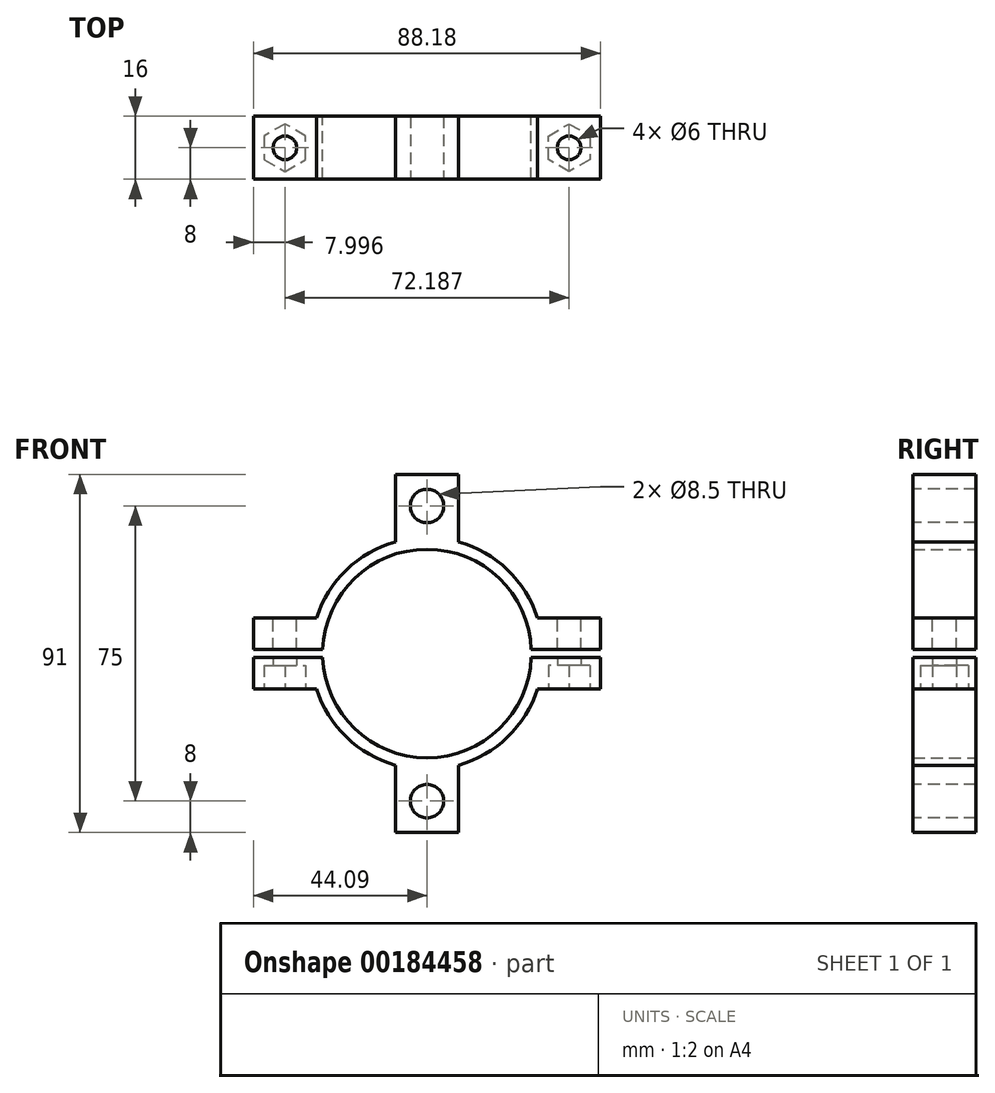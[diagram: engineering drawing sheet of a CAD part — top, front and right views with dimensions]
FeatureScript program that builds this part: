
annotation { "Feature Type Name" : "Feature", "Feature Type Description" : "" }
export const myFeature = defineFeature(function(context is Context, id is Id, definition is map)
    precondition{}
    {
        {
            var Q0;
            Q0=qCreatedBy(makeId("Front.planeOp"),FACE);
            var sketch = newSketch(context, id + "F0", { "sketchPlane" : qUnion([Q0])});
            skCircle(sketch, "E0", {"center": v(0, 0) * mm, "radius": 26.5 * mm, "construction": true});
            skLineSegment(sketch, "E1", {"start": v(-8, -45.5) * mm, "end": v(-8, -28.4) * mm});
            skArc(sketch, "E2", {"start": v(0, -26.5) * mm, "mid": v(-18.38, -19.09) * mm, "end": v(-26.48, -1) * mm});
            skLineSegment(sketch, "E3", {"start": v(-26.48, -1) * mm, "end": v(-44.1, -1) * mm});
            skLineSegment(sketch, "E4", {"start": v(-44.1, -1) * mm, "end": v(-44.1, -9) * mm});
            skLineSegment(sketch, "E5", {"start": v(-44.1, -9) * mm, "end": v(-28.1, -9) * mm});
            skArc(sketch, "E6", {"start": v(-28.1, -9) * mm, "mid": v(-20.49, -21.23) * mm, "end": v(-8, -28.4) * mm});
            skLineSegment(sketch, "E7", {"start": v(0, 0) * mm, "end": v(0, -39.44) * mm, "construction": true});
            skLineSegment(sketch, "E8", {"start": v(0, -45.5) * mm, "end": v(0, -26.5) * mm});
            skLineSegment(sketch, "E9", {"start": v(-8, -45.5) * mm, "end": v(0, -45.5) * mm});
            skSolve(sketch);
        }
        {
            var Q0;
            Q0=makeQuery(id+"F0.imprint","IMPRINT",FACE,{"disambiguationData":[TD([[makeQuery(id+"F0.imprint","IMPRINT",EDGE,{"derivedFrom":sQuery(id+"F0.wireOp",EDGE,"E1")}),-1.0]])]});
            extrude(context, id + "F1", {"entities" : qUnion([Q0]), "depth" : 16 * mm});
        }
        {
            var Q0;
            Q0=makeQuery(id+"F1.opExtrude","SWEPT_FACE",FACE,{"disambiguationData":[OSD([sQuery(id+"F0.wireOp",EDGE,"E5")])]});
            var sketch = newSketch(context, id + "F2", { "sketchPlane" : qUnion([Q0])});
            skLineSegment(sketch, "E10", {"start": v(-28.1, 8) * mm, "end": v(-44.1, 8) * mm, "construction": true});
            skLineSegment(sketch, "E11", {"start": v(-36.1, 16) * mm, "end": v(-36.1, 0) * mm, "construction": true});
            skCircle(sketch, "E12.cCircle", {"center": v(-36.1, 8) * mm, "radius": 5.25 * mm, "construction": true});
            skLineSegment(sketch, "E12.0", {"start": v(-36.1, 14.06) * mm, "end": v(-30.84, 11.03) * mm});
            skLineSegment(sketch, "E12.1", {"start": v(-30.84, 11.03) * mm, "end": v(-30.84, 4.97) * mm});
            skLineSegment(sketch, "E12.2", {"start": v(-30.84, 4.97) * mm, "end": v(-36.1, 1.94) * mm});
            skLineSegment(sketch, "E12.3", {"start": v(-36.1, 1.94) * mm, "end": v(-41.34, 4.97) * mm});
            skLineSegment(sketch, "E12.4", {"start": v(-41.34, 4.97) * mm, "end": v(-41.34, 11.03) * mm});
            skLineSegment(sketch, "E12.5", {"start": v(-41.34, 11.03) * mm, "end": v(-36.1, 14.06) * mm});
            skPoint(sketch, "E12.0.midPoint", {"position": v(-33.47, 12.55) * mm});
            skSolve(sketch);
        }
        {
            var Q0;
            Q0 = qSketchRegion(id + "F2", true);
            extrude(context, id + "F3", {"entities" : qUnion([Q0]), "operationType" : NewBodyOperationType.REMOVE, "oppositeDirection" : true, "depth" : 6 * mm});
        }
        {
            var Q0;
            Q0=makeQuery(id+"F3.boolean.opBoolean","COPY",FACE,{"derivedFrom":makeQuery(id+"F3.opExtrude","CAP_FACE",FACE,{"disambiguationData":[OSD([sQuery(id+"F2.wireOp",EDGE,"E12.0"),sQuery(id+"F2.wireOp",EDGE,"E12.1"),sQuery(id+"F2.wireOp",EDGE,"E12.2"),sQuery(id+"F2.wireOp",EDGE,"E12.3"),sQuery(id+"F2.wireOp",EDGE,"E12.4"),sQuery(id+"F2.wireOp",EDGE,"E12.5")])],"isStart":false})});
            var sketch = newSketch(context, id + "F4", { "sketchPlane" : qUnion([Q0])});
            skLineSegment(sketch, "E13", {"start": v(-30.84, 8) * mm, "end": v(-41.34, 8) * mm, "construction": true});
            skLineSegment(sketch, "E14", {"start": v(-36.1, 14.06) * mm, "end": v(-36.1, 1.94) * mm, "construction": true});
            skPoint(sketch, "E15", {"position": v(-36.1, 8) * mm});
            skSolve(sketch);
        }
        {
            var Q0;
            Q0=sQuery(id+"F4.wireOp",VERTEX,"E15");
            var Q1;
            Q1=makeQuery(id+"F1.opExtrude","SWEPT_BODY",BODY,{"disambiguationData":[OSD([sQuery(id+"F0.wireOp",EDGE,"LuoD2EtT-gfBr-CX7n-iTLg-iMxV0IS75IWG"),sQuery(id+"F0.wireOp",EDGE,"0Tmr8PXh-Ax4I-PApt-1Kwb-XwLZEwwx8Ye0"),sQuery(id+"F0.wireOp",EDGE,"TVMvmqPK-jYpf-7Blp-NSc2-0YLIsRcv3KJq"),sQuery(id+"F0.wireOp",EDGE,"E1"),sQuery(id+"F0.wireOp",EDGE,"E2"),sQuery(id+"F0.wireOp",EDGE,"E3"),sQuery(id+"F0.wireOp",EDGE,"E4"),sQuery(id+"F0.wireOp",EDGE,"E5"),sQuery(id+"F0.wireOp",EDGE,"E6"),sQuery(id+"F0.wireOp",EDGE,"E8")])]});
            hole(context, id + "F5", {"style" : HoleStyle.SIMPLE, "endStyle" : HoleEndStyle.BLIND, "holeDiameter" : 6 * mm, "holeDepth" : 7 * mm, "locations" : qUnion([Q0]), "scope" : qUnion([Q1])});
        }
        {
            var Q0;
            Q0=makeQuery(id+"F1.opExtrude","SWEPT_BODY",BODY,{"disambiguationData":[OSD([sQuery(id+"F0.wireOp",EDGE,"LuoD2EtT-gfBr-CX7n-iTLg-iMxV0IS75IWG"),sQuery(id+"F0.wireOp",EDGE,"0Tmr8PXh-Ax4I-PApt-1Kwb-XwLZEwwx8Ye0"),sQuery(id+"F0.wireOp",EDGE,"TVMvmqPK-jYpf-7Blp-NSc2-0YLIsRcv3KJq"),sQuery(id+"F0.wireOp",EDGE,"E1"),sQuery(id+"F0.wireOp",EDGE,"E2"),sQuery(id+"F0.wireOp",EDGE,"E3"),sQuery(id+"F0.wireOp",EDGE,"E4"),sQuery(id+"F0.wireOp",EDGE,"E5"),sQuery(id+"F0.wireOp",EDGE,"E6"),sQuery(id+"F0.wireOp",EDGE,"E8")])]});
            var Q1;
            Q1=makeQuery(id+"F1.opExtrude","SWEPT_FACE",FACE,{"disambiguationData":[OSD([sQuery(id+"F0.wireOp",EDGE,"E8")])]});
            mirror(context, id + "F6", {"operationType" : NewBodyOperationType.ADD, "entities" : qUnion([Q0]), "mirrorPlane" : qUnion([Q1])});
        }
        {
            var Q0;
            {var subQ0=makeQuery(id+"F1.opExtrude","CAP_FACE",FACE,{"disambiguationData":[OSD([sQuery(id+"F0.wireOp",EDGE,"E1"),sQuery(id+"F0.wireOp",EDGE,"E2"),sQuery(id+"F0.wireOp",EDGE,"E3"),sQuery(id+"F0.wireOp",EDGE,"E4"),sQuery(id+"F0.wireOp",EDGE,"E5"),sQuery(id+"F0.wireOp",EDGE,"E6"),sQuery(id+"F0.wireOp",EDGE,"E8"),sQuery(id+"F0.wireOp",EDGE,"E9")])],"isStart":false});Q0=makeQuery(id+"F6.boolean.opBoolean","MERGE",FACE,{"derivedFrom":[subQ0,makeQuery(id+"F6.opPattern","COPY",FACE,{"derivedFrom":subQ0,"instanceName":"1"})]});}
            var sketch = newSketch(context, id + "F7", { "sketchPlane" : qUnion([Q0])});
            skLineSegment(sketch, "E16", {"start": v(0, 0) * mm, "end": v(0, -37.5) * mm, "construction": true});
            skSolve(sketch);
        }
        {
            var Q0;
            Q0=sQuery(id+"F7.wireOp",VERTEX,"E16.end");
            var Q1;
            Q1=makeQuery(id+"F1.opExtrude","SWEPT_BODY",BODY,{"disambiguationData":[OSD([sQuery(id+"F0.wireOp",EDGE,"E1"),sQuery(id+"F0.wireOp",EDGE,"E2"),sQuery(id+"F0.wireOp",EDGE,"E3"),sQuery(id+"F0.wireOp",EDGE,"E4"),sQuery(id+"F0.wireOp",EDGE,"E5"),sQuery(id+"F0.wireOp",EDGE,"E6"),sQuery(id+"F0.wireOp",EDGE,"E8"),sQuery(id+"F0.wireOp",EDGE,"E9")])]});
            hole(context, id + "F8", {"style" : HoleStyle.SIMPLE, "endStyle" : HoleEndStyle.THROUGH, "holeDiameter" : 8.5 * mm, "locations" : qUnion([Q0]), "scope" : qUnion([Q1]), "isTappedThrough" : true});
        }
        {
            var Q0;
            Q0=makeQuery(id+"F1.opExtrude","SWEPT_BODY",BODY,{"disambiguationData":[OSD([sQuery(id+"F0.wireOp",EDGE,"E1"),sQuery(id+"F0.wireOp",EDGE,"E2"),sQuery(id+"F0.wireOp",EDGE,"E3"),sQuery(id+"F0.wireOp",EDGE,"E4"),sQuery(id+"F0.wireOp",EDGE,"E5"),sQuery(id+"F0.wireOp",EDGE,"E6"),sQuery(id+"F0.wireOp",EDGE,"E8"),sQuery(id+"F0.wireOp",EDGE,"E9")])]});
            var Q1;
            Q1=qCreatedBy(makeId("Top.planeOp"),FACE);
            mirror(context, id + "F9", {"entities" : qUnion([Q0]), "mirrorPlane" : qUnion([Q1])});
        }
        {
            var Q0;
            Q0=makeQuery(id+"F9.opPattern","COPY",FACE,{"derivedFrom":makeQuery(id+"F3.boolean.opBoolean","COPY",FACE,{"derivedFrom":makeQuery(id+"F3.opExtrude","CAP_FACE",FACE,{"disambiguationData":[OSD([sQuery(id+"F2.wireOp",EDGE,"E12.0"),sQuery(id+"F2.wireOp",EDGE,"E12.1"),sQuery(id+"F2.wireOp",EDGE,"E12.2"),sQuery(id+"F2.wireOp",EDGE,"E12.3"),sQuery(id+"F2.wireOp",EDGE,"E12.4"),sQuery(id+"F2.wireOp",EDGE,"E12.5")])],"isStart":false})}),"instanceName":"1"});
            var sketch = newSketch(context, id + "F10", { "sketchPlane" : qUnion([Q0])});
            skLineSegment(sketch, "E17.0.0", {"start": v(-36.1, -14.06) * mm, "end": v(-30.84, -11.03) * mm});
            skLineSegment(sketch, "E17.0.1", {"start": v(-30.84, -11.03) * mm, "end": v(-30.84, -4.97) * mm});
            skLineSegment(sketch, "E17.0.2", {"start": v(-30.84, -4.97) * mm, "end": v(-36.1, -1.94) * mm});
            skLineSegment(sketch, "E17.0.3", {"start": v(-36.1, -1.94) * mm, "end": v(-41.34, -4.97) * mm});
            skLineSegment(sketch, "E17.0.4", {"start": v(-41.34, -4.97) * mm, "end": v(-41.34, -11.03) * mm});
            skLineSegment(sketch, "E17.0.5", {"start": v(-41.34, -11.03) * mm, "end": v(-36.1, -14.06) * mm});
            skLineSegment(sketch, "E18.0.0", {"start": v(30.84, -11.03) * mm, "end": v(36.1, -14.06) * mm});
            skLineSegment(sketch, "E18.0.1", {"start": v(36.1, -14.06) * mm, "end": v(41.34, -11.03) * mm});
            skLineSegment(sketch, "E18.0.2", {"start": v(41.34, -11.03) * mm, "end": v(41.34, -4.97) * mm});
            skLineSegment(sketch, "E18.0.3", {"start": v(41.34, -4.97) * mm, "end": v(36.1, -1.94) * mm});
            skLineSegment(sketch, "E18.0.4", {"start": v(36.1, -1.94) * mm, "end": v(30.84, -4.97) * mm});
            skLineSegment(sketch, "E18.0.5", {"start": v(30.84, -4.97) * mm, "end": v(30.84, -11.03) * mm});
            skSolve(sketch);
        }
        {
            var Q0;
            Q0=makeQuery(id+"F10.imprint","IMPRINT",FACE,{"disambiguationData":[TD([[makeQuery(id+"F10.imprint","IMPRINT",EDGE,{"derivedFrom":sQuery(id+"F10.wireOp",EDGE,"E17.0.0")}),1.0]])]});
            var Q1;
            Q1=makeQuery(id+"F9.opPattern","COPY",FACE,{"derivedFrom":makeQuery(id+"F1.opExtrude","SWEPT_FACE",FACE,{"disambiguationData":[OSD([sQuery(id+"F0.wireOp",EDGE,"E5")])]}),"instanceName":"1"});
            extrude(context, id + "F11", {"entities" : qUnion([Q0]), "operationType" : NewBodyOperationType.ADD, "endBound" : BoundingType.UP_TO_SURFACE, "endBoundEntityFace" : qUnion([Q1]), "depth" : 25 * mm});
        }
        {
            var Q0;
            Q0=makeQuery(id+"F9.opPattern","COPY",FACE,{"derivedFrom":makeQuery(id+"F6.opPattern","COPY",FACE,{"derivedFrom":makeQuery(id+"F3.boolean.opBoolean","COPY",FACE,{"derivedFrom":makeQuery(id+"F3.opExtrude","CAP_FACE",FACE,{"disambiguationData":[OSD([sQuery(id+"F2.wireOp",EDGE,"E12.0"),sQuery(id+"F2.wireOp",EDGE,"E12.1"),sQuery(id+"F2.wireOp",EDGE,"E12.2"),sQuery(id+"F2.wireOp",EDGE,"E12.3"),sQuery(id+"F2.wireOp",EDGE,"E12.4"),sQuery(id+"F2.wireOp",EDGE,"E12.5")])],"isStart":false})}),"instanceName":"1"}),"instanceName":"1"});
            var Q1;
            Q1=makeQuery(id+"F9.opPattern","COPY",FACE,{"derivedFrom":makeQuery(id+"F6.opPattern","COPY",FACE,{"derivedFrom":makeQuery(id+"F1.opExtrude","SWEPT_FACE",FACE,{"disambiguationData":[OSD([sQuery(id+"F0.wireOp",EDGE,"E5")])]}),"instanceName":"1"}),"instanceName":"1"});
            extrude(context, id + "F12", {"entities" : qUnion([Q0]), "operationType" : NewBodyOperationType.ADD, "endBound" : BoundingType.UP_TO_SURFACE, "endBoundEntityFace" : qUnion([Q1]), "depth" : 25 * mm});
        }
    });
